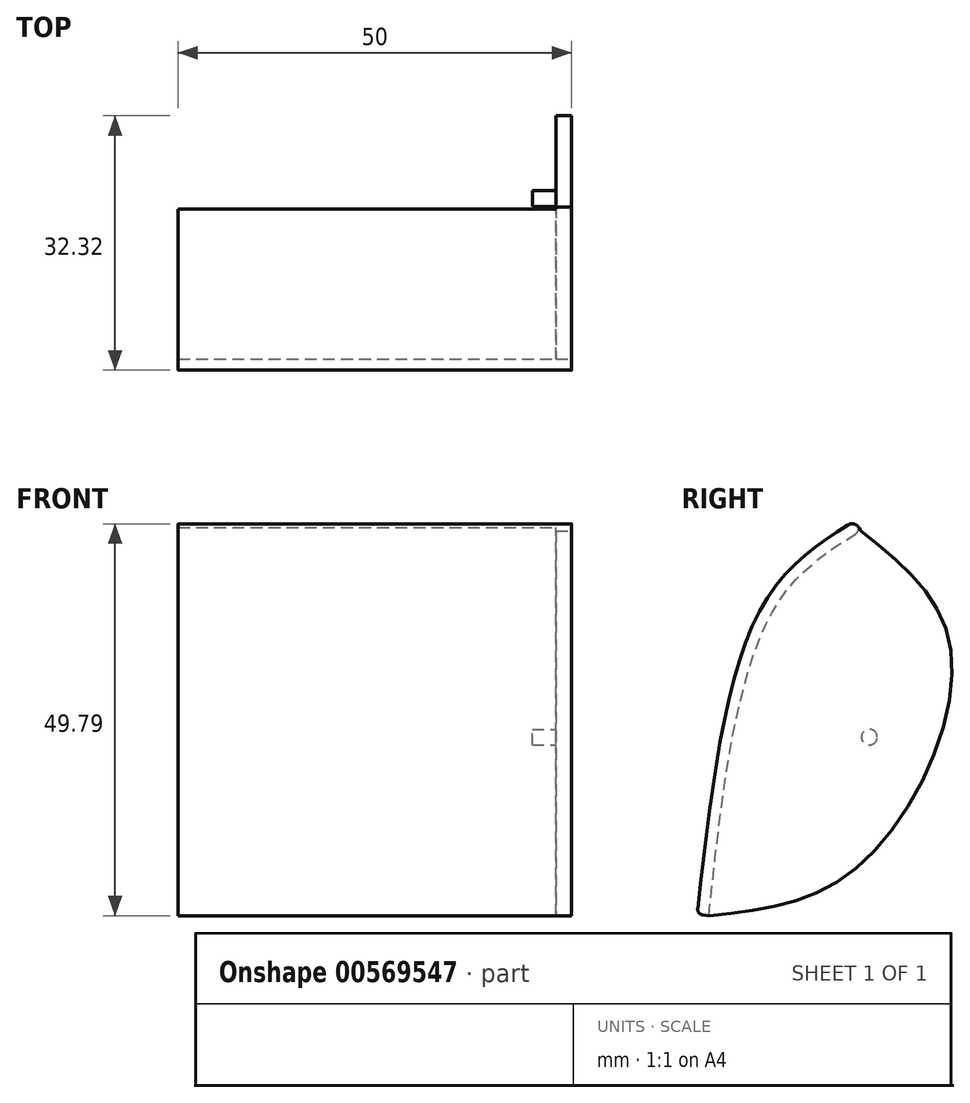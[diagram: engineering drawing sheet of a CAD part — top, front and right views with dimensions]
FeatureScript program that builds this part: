
annotation { "Feature Type Name" : "Feature", "Feature Type Description" : "" }
export const myFeature = defineFeature(function(context is Context, id is Id, definition is map)
    precondition{}
    {
        {
            var Q0;
            Q0=qCreatedBy(makeId("Right.planeOp"),FACE);
            var sketch = newSketch(context, id + "F0", { "sketchPlane" : qUnion([Q0])});
            skFitSpline(sketch, "E0", {"points": [v(0, 0) * mm, v(8.29, 39.13) * mm, v(20, 50) * mm], "startDerivative": vector(8.4, 74.82) * mm, "endDerivative": vector(33.48, 21.15) * mm});
            skFitSpline(sketch, "E1.0", {"points": [v(1.5, -0.17) * mm, v(1.84, 2.95) * mm, v(2.54, 9.17) * mm, v(3.74, 18.14) * mm, v(5, 25) * mm, v(6.24, 29.94) * mm, v(7.3, 33.32) * mm, v(8.3, 35.84) * mm, v(9.17, 37.64) * mm, v(10.1, 39.3) * mm, v(11.35, 41.1) * mm, v(13.01, 42.98) * mm, v(14.8, 44.6) * mm, v(17.35, 46.55) * mm, v(19.4, 47.85) * mm, v(20.8, 48.73) * mm]});
            skLineSegment(sketch, "E2", {"start": v(20, 50) * mm, "end": v(20.8, 48.73) * mm});
            skLineSegment(sketch, "E3", {"start": v(1.5, -0.17) * mm, "end": v(0.75, -0.08) * mm});
            skLineSegment(sketch, "E4.filletArc", {"start": v(1.5, -0.17) * mm, "end": v(1.5, -0.17) * mm});
            skArc(sketch, "E5.filletArc", {"start": v(0.08, 0.75) * mm, "mid": v(0.24, 0.2) * mm, "end": v(0.75, -0.08) * mm});
            skPoint(sketch, "E6.visualSharp", {"position": v(20.8, 48.73) * mm});
            skLineSegment(sketch, "E6.filletArc", {"start": v(20.8, 48.73) * mm, "end": v(20.8, 48.73) * mm});
            skLineSegment(sketch, "E7.filletArc", {"start": v(20, 50) * mm, "end": v(20, 50) * mm});
            skCircle(sketch, "E8", {"center": v(21.88, 22.51) * mm, "radius": 1 * mm});
            skFitSpline(sketch, "E9", {"points": [v(20.8, 48.73) * mm, v(32.25, 33.49) * mm, v(20.8, 6.33) * mm, v(1.5, -0.17) * mm], "startDerivative": vector(51.82, -41.39) * mm, "endDerivative": vector(-64.23, -6.62) * mm});
            skSolve(sketch);
        }
        {
            var Q0;
            Q0=makeQuery(id+"F0.imprint","IMPRINT",FACE,{"disambiguationData":[TD([[makeQuery(id+"F0.imprint","IMPRINT",EDGE,{"derivedFrom":sQuery(id+"F0.wireOp",EDGE,"E0")}),-1.0]])]});
            extrude(context, id + "F1", {"entities" : qUnion([Q0]), "oppositeDirection" : true, "depth" : 50 * mm, "offsetDistance" : 25 * mm});
        }
        {
            var Q0;
            Q0=makeQuery(id+"F0.imprint","IMPRINT",FACE,{"disambiguationData":[TD([[makeQuery(id+"F0.imprint","IMPRINT",EDGE,{"derivedFrom":sQuery(id+"F0.wireOp",EDGE,"E1.0")}),-1.0]])]});
            var Q1;
            Q1=makeQuery(id+"F0.imprint","IMPRINT",FACE,{"disambiguationData":[TD([[makeQuery(id+"F0.imprint","IMPRINT",EDGE,{"derivedFrom":sQuery(id+"F0.wireOp",EDGE,"E8")}),1.0]])]});
            extrude(context, id + "F2", {"entities" : qUnion([Q0, Q1]), "operationType" : NewBodyOperationType.ADD, "oppositeDirection" : true, "depth" : 2 * mm, "offsetDistance" : 25 * mm});
        }
        {
            var Q0;
            Q0=makeQuery(id+"F0.imprint","IMPRINT",FACE,{"disambiguationData":[TD([[makeQuery(id+"F0.imprint","IMPRINT",EDGE,{"derivedFrom":sQuery(id+"F0.wireOp",EDGE,"E8")}),1.0]])]});
            extrude(context, id + "F3", {"entities" : qUnion([Q0]), "operationType" : NewBodyOperationType.ADD, "oppositeDirection" : true, "depth" : 5 * mm, "offsetDistance" : 25 * mm});
        }
        {
            var Q0;
            Q0=makeQuery(id+"F1.opExtrude","SWEPT_EDGE",EDGE,{"disambiguationData":[OSD([sQuery(id+"F0.wireOp",EDGE,"E0"),sQuery(id+"F0.wireOp",EDGE,"E2")])]});
            fillet(context, id + "F4", {"entities" : qUnion([Q0]), "radius" : 1 * mm, "tangentPropagation" : true, "allowEdgeOverflow" : false});
        }
        {
            var Q0;
            Q0=makeQuery(id+"F2.boolean.opBoolean","SPLIT",EDGE,{"derivedFrom":makeQuery(id+"F1.opExtrude","SWEPT_EDGE",EDGE,{"disambiguationData":[OSD([sQuery(id+"F0.wireOp",EDGE,"E1.0"),sQuery(id+"F0.wireOp",EDGE,"E2"),sQuery(id+"F0.wireOp",EDGE,"E9")])]})});
            fillet(context, id + "F5", {"entities" : qUnion([Q0]), "radius" : 1 * mm, "tangentPropagation" : true, "allowEdgeOverflow" : false});
        }
    });
